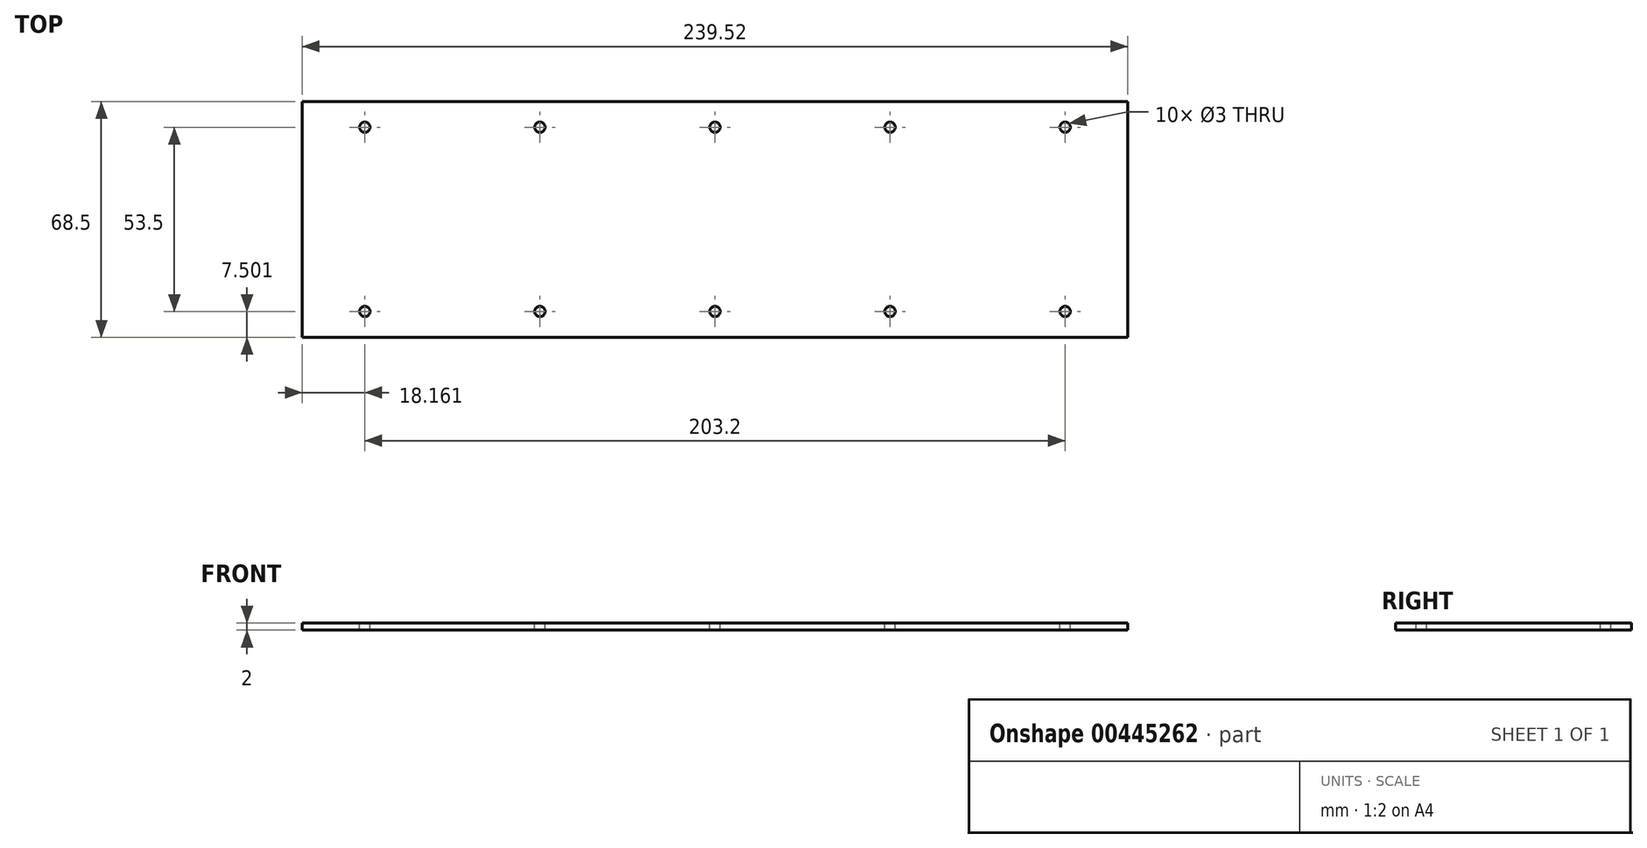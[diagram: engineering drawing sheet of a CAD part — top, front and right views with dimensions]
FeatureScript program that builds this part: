
annotation { "Feature Type Name" : "Feature", "Feature Type Description" : "" }
export const myFeature = defineFeature(function(context is Context, id is Id, definition is map)
    precondition{}
    {
        {
            var Q0;
            Q0=qCreatedBy(makeId("Top.planeOp"),FACE);
            var sketch = newSketch(context, id + "F0", { "sketchPlane" : qUnion([Q0])});
            skLineSegment(sketch, "E0.bottom", {"start": v(-102.06, 9.02) * mm, "end": v(137.46, 9.02) * mm});
            skLineSegment(sketch, "E0.top", {"start": v(-102.06, -59.48) * mm, "end": v(137.46, -59.48) * mm});
            skLineSegment(sketch, "E0.left", {"start": v(-102.06, 9.02) * mm, "end": v(-102.06, -59.48) * mm});
            skLineSegment(sketch, "E0.right", {"start": v(137.46, 9.02) * mm, "end": v(137.46, -59.48) * mm});
            skSolve(sketch);
        }
        {
            var Q0;
            Q0 = qSketchRegion(id + "F0", true);
            extrude(context, id + "F1", {"entities" : qUnion([Q0]), "depth" : 2 * mm});
        }
        {
            var Q0;
            Q0=makeQuery(id+"F1.opExtrude","CAP_FACE",FACE,{"disambiguationData":[OSD([sQuery(id+"F0.wireOp",EDGE,"E0.bottom"),sQuery(id+"F0.wireOp",EDGE,"E0.top"),sQuery(id+"F0.wireOp",EDGE,"E0.left"),sQuery(id+"F0.wireOp",EDGE,"E0.right")])],"isStart":false});
            var sketch = newSketch(context, id + "F2", { "sketchPlane" : qUnion([Q0])});
            skLineSegment(sketch, "E1", {"start": v(-103.4, 1.52) * mm, "end": v(112.3, 1.52) * mm});
            skLineSegment(sketch, "E2", {"start": v(-82.18, 1.52) * mm, "end": v(-82.18, 9.02) * mm});
            skCircle(sketch, "E3", {"center": v(-83.9, 1.52) * mm, "radius": 1.5 * mm});
            skCircle(sketch, "E4.1.0.0", {"center": v(-33.1, 1.52) * mm, "radius": 1.5 * mm});
            skCircle(sketch, "E4.2.0.0", {"center": v(17.7, 1.52) * mm, "radius": 1.5 * mm});
            skCircle(sketch, "E4.3.0.0", {"center": v(68.5, 1.52) * mm, "radius": 1.5 * mm});
            skCircle(sketch, "E4.4.0.0", {"center": v(119.3, 1.52) * mm, "radius": 1.5 * mm});
            skLineSegment(sketch, "E4.direction1", {"start": v(-83.9, 1.52) * mm, "end": v(-33.1, 1.52) * mm, "construction": true});
            skLineSegment(sketch, "E5", {"start": v(17.7, 9.02) * mm, "end": v(17.7, -59.48) * mm, "construction": true});
            skLineSegment(sketch, "E6", {"start": v(0, 0) * mm, "end": v(2.92, 0) * mm});
            skLineSegment(sketch, "E7", {"start": v(-102.06, -25.23) * mm, "end": v(137.46, -25.23) * mm});
            skCircle(sketch, "E8.MirrorC", {"center": v(119.3, -51.98) * mm, "radius": 1.5 * mm});
            skCircle(sketch, "E9.MirrorC", {"center": v(68.5, -51.98) * mm, "radius": 1.5 * mm});
            skCircle(sketch, "E10.MirrorC", {"center": v(17.7, -51.98) * mm, "radius": 1.5 * mm});
            skCircle(sketch, "E11.MirrorC", {"center": v(-33.1, -51.98) * mm, "radius": 1.5 * mm});
            skCircle(sketch, "E12.MirrorC", {"center": v(-83.9, -51.98) * mm, "radius": 1.5 * mm});
            skSolve(sketch);
        }
        {
            var Q0;
            Q0 = qSketchRegion(id + "F2", true);
            extrude(context, id + "F3", {"entities" : qUnion([Q0]), "operationType" : NewBodyOperationType.REMOVE, "endBound" : BoundingType.THROUGH_ALL, "oppositeDirection" : true, "depth" : 25.4 * mm});
        }
    });
